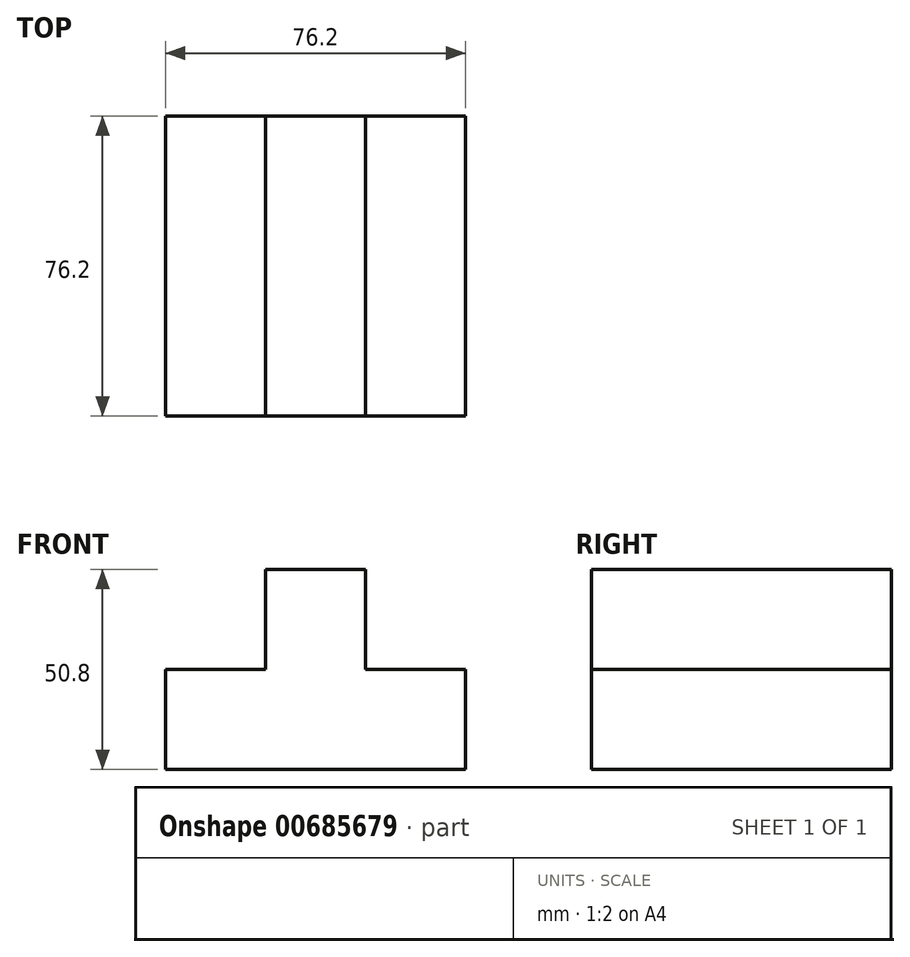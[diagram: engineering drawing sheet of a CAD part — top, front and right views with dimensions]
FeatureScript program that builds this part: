
annotation { "Feature Type Name" : "Feature", "Feature Type Description" : "" }
export const myFeature = defineFeature(function(context is Context, id is Id, definition is map)
    precondition{}
    {
        {
            var Q0;
            Q0=qCreatedBy(makeId("Front.planeOp"),FACE);
            var sketch = newSketch(context, id + "F0", { "sketchPlane" : qUnion([Q0])});
            skLineSegment(sketch, "E0", {"start": v(-40.86, -25.4) * mm, "end": v(-40.86, 0) * mm});
            skLineSegment(sketch, "E1", {"start": v(-40.86, 0) * mm, "end": v(-15.46, 0) * mm});
            skLineSegment(sketch, "E2", {"start": v(-15.46, 0) * mm, "end": v(-15.46, 25.4) * mm});
            skLineSegment(sketch, "E3", {"start": v(-15.46, 25.4) * mm, "end": v(9.94, 25.4) * mm});
            skLineSegment(sketch, "E4", {"start": v(9.94, 25.4) * mm, "end": v(9.94, 0) * mm});
            skLineSegment(sketch, "E5", {"start": v(9.94, 0) * mm, "end": v(35.34, 0) * mm});
            skLineSegment(sketch, "E6", {"start": v(35.34, 0) * mm, "end": v(35.34, -25.4) * mm});
            skLineSegment(sketch, "E7", {"start": v(35.34, -25.4) * mm, "end": v(-40.86, -25.4) * mm});
            skSolve(sketch);
        }
        {
            var Q0;
            Q0 = qSketchRegion(id + "F0", true);
            extrude(context, id + "F1", {"entities" : qUnion([Q0]), "depth" : 76.2 * mm, "offsetDistance" : 25.4 * mm});
        }
    });
